FCSTD DOCUMENT  (FreeCAD 1.0R39109 (Git))
Label: 2020v
License: All rights reserved
LicenseURL: https://en.wikipedia.org/wiki/All_rights_reserved
objects: Sketcher::SketchObject×1
note: 2 computed .brp shape members not serialized (recipe doc carries the construction recipe); baked Part::Feature solids carry a one-line shape summary decoded from their .brp

FEATURE [Sketcher::SketchObject] Sketch
  ArcFitTolerance = 1e-06
  FullyConstrained = false
  MakeInternals = false
  sketch-geometry (57):
    g0: ArcOfCircle CenterX=-9.49927 CenterY=-9.49965 CenterZ=0 NormalX=0 NormalY=0 NormalZ=1 AngleXU=0 Radius=0.5 StartAngle=3.14159 EndAngle=4.71239
    g1: LineSegment StartX=-9.49927 StartY=-9.99965 StartZ=0 EndX=-4.57927 EndY=-9.99965 EndZ=0
    g2: LineSegment StartX=-4.57927 StartY=-9.99965 StartZ=0 EndX=-3.12427 EndY=-8.54465 EndZ=0
    g3: LineSegment StartX=-3.12427 StartY=-8.54465 StartZ=0 EndX=-3.12427 EndY=-8.19465 EndZ=0
    g4: LineSegment StartX=-3.12427 StartY=-8.19465 StartZ=0 EndX=-5.49927 EndY=-8.19465 EndZ=0
    g5: LineSegment StartX=-5.49927 StartY=-8.19465 StartZ=0 EndX=-5.49927 EndY=-6.55465 EndZ=0
    g6: LineSegment StartX=-5.49927 StartY=-6.55465 StartZ=0 EndX=-2.84427 EndY=-3.89965 EndZ=0
    g7: LineSegment StartX=-2.84427 StartY=-3.89965 StartZ=0 EndX=2.84573 EndY=-3.89965 EndZ=0
    g8: LineSegment StartX=2.84573 StartY=-3.89965 StartZ=0 EndX=5.50073 EndY=-6.55465 EndZ=0
    g9: LineSegment StartX=5.50073 StartY=-6.55465 StartZ=0 EndX=5.50073 EndY=-8.19465 EndZ=0
    g10: LineSegment StartX=5.50073 StartY=-8.19465 StartZ=0 EndX=3.12573 EndY=-8.19465 EndZ=0
    g11: LineSegment StartX=3.12573 StartY=-8.19465 StartZ=0 EndX=3.12573 EndY=-8.54465 EndZ=0
    g12: LineSegment StartX=3.12573 StartY=-8.54465 StartZ=0 EndX=4.58073 EndY=-9.99965 EndZ=0
    g13: LineSegment StartX=4.58073 StartY=-9.99965 StartZ=0 EndX=9.50073 EndY=-9.99965 EndZ=0
    g14: ArcOfCircle CenterX=9.50073 CenterY=-9.49965 CenterZ=0 NormalX=0 NormalY=0 NormalZ=1 AngleXU=0 Radius=0.5 StartAngle=4.71239 EndAngle=6.28319
    g15: LineSegment StartX=10.0007 StartY=-9.49965 StartZ=0 EndX=10.0007 EndY=-4.57965 EndZ=0
    g16: LineSegment StartX=10.0007 StartY=-4.57965 StartZ=0 EndX=8.54573 EndY=-3.12465 EndZ=0
    g17: LineSegment StartX=8.54573 StartY=-3.12465 StartZ=0 EndX=8.19573 EndY=-3.12465 EndZ=0
    g18: LineSegment StartX=8.19573 StartY=-3.12465 StartZ=0 EndX=8.19573 EndY=-5.48833 EndZ=0
    g19: LineSegment StartX=8.19573 StartY=-5.48833 StartZ=0 EndX=6.55573 EndY=-5.48833 EndZ=0
    g20: LineSegment StartX=6.55573 StartY=-5.48833 StartZ=0 EndX=3.90073 EndY=-2.83333 EndZ=0
    g21: LineSegment StartX=3.90073 StartY=-2.83333 StartZ=0 EndX=3.90073 EndY=2.83403 EndZ=0
    g22: LineSegment StartX=3.90073 StartY=2.83403 StartZ=0 EndX=6.55573 EndY=5.48903 EndZ=0
    g23: LineSegment StartX=6.55573 StartY=5.48903 StartZ=0 EndX=8.19573 EndY=5.48903 EndZ=0
    g24: LineSegment StartX=8.19573 StartY=5.48903 StartZ=0 EndX=8.20867 EndY=3.12535 EndZ=0
    g25: LineSegment StartX=8.20867 StartY=3.12535 StartZ=0 EndX=8.54573 EndY=3.12535 EndZ=0
    g26: LineSegment StartX=8.54573 StartY=3.12535 StartZ=0 EndX=10.0007 EndY=4.58035 EndZ=0
    g27: LineSegment StartX=10.0007 StartY=4.58035 StartZ=0 EndX=10.0007 EndY=9.50035 EndZ=0
    g28: ArcOfCircle CenterX=9.50073 CenterY=9.50035 CenterZ=0 NormalX=0 NormalY=0 NormalZ=1 AngleXU=0 Radius=0.5 StartAngle=0 EndAngle=1.5708
    g29: LineSegment StartX=9.50073 StartY=10.0003 StartZ=0 EndX=4.58073 EndY=10.0003 EndZ=0
    g30: LineSegment StartX=4.58073 StartY=10.0003 StartZ=0 EndX=3.12573 EndY=8.54535 EndZ=0
    g31: LineSegment StartX=3.12573 StartY=8.54535 StartZ=0 EndX=3.12573 EndY=8.19535 EndZ=0
    g32: LineSegment StartX=3.12573 StartY=8.19535 StartZ=0 EndX=5.50073 EndY=8.19535 EndZ=0
    g33: LineSegment StartX=5.50073 StartY=8.19535 StartZ=0 EndX=5.50073 EndY=6.55535 EndZ=0
    g34: LineSegment StartX=5.50073 StartY=6.55535 StartZ=0 EndX=2.84573 EndY=3.90035 EndZ=0
    g35: LineSegment StartX=2.84573 StartY=3.90035 StartZ=0 EndX=-2.84427 EndY=3.90035 EndZ=0
    g36: LineSegment StartX=-2.84427 StartY=3.90035 StartZ=0 EndX=-5.49927 EndY=6.55535 EndZ=0
    g37: LineSegment StartX=-5.49927 StartY=6.55535 StartZ=0 EndX=-5.49927 EndY=8.19535 EndZ=0
    g38: LineSegment StartX=-5.49927 StartY=8.19535 StartZ=0 EndX=-3.12427 EndY=8.19535 EndZ=0
    g39: LineSegment StartX=-3.12427 StartY=8.19535 StartZ=0 EndX=-3.12427 EndY=8.54535 EndZ=0
    g40: LineSegment StartX=-3.12427 StartY=8.54535 StartZ=0 EndX=-4.57927 EndY=10.0003 EndZ=0
    g41: LineSegment StartX=-4.57927 StartY=10.0003 StartZ=0 EndX=-9.49927 EndY=10.0003 EndZ=0
    g42: ArcOfCircle CenterX=-9.49927 CenterY=9.50035 CenterZ=0 NormalX=0 NormalY=0 NormalZ=1 AngleXU=0 Radius=0.5 StartAngle=1.5708 EndAngle=3.14159
    g43: LineSegment StartX=-9.99927 StartY=9.50035 StartZ=0 EndX=-9.99927 EndY=4.58035 EndZ=0
    g44: LineSegment StartX=-9.99927 StartY=4.58035 StartZ=0 EndX=-8.54427 EndY=3.12535 EndZ=0
    g45: LineSegment StartX=-8.54427 StartY=3.12535 StartZ=0 EndX=-8.19427 EndY=3.12535 EndZ=0
    g46: LineSegment StartX=-8.19427 StartY=3.12535 StartZ=0 EndX=-8.19427 EndY=5.48903 EndZ=0
    g47: LineSegment StartX=-8.19427 StartY=5.48903 StartZ=0 EndX=-6.55427 EndY=5.48903 EndZ=0
    g48: LineSegment StartX=-6.55427 StartY=5.48903 StartZ=0 EndX=-3.89927 EndY=2.83403 EndZ=0
    g49: LineSegment StartX=-3.89927 StartY=2.83403 StartZ=0 EndX=-3.89927 EndY=-2.83333 EndZ=0
    g50: LineSegment StartX=-3.89927 StartY=-2.83333 StartZ=0 EndX=-6.55427 EndY=-5.48833 EndZ=0
    g51: LineSegment StartX=-6.55427 StartY=-5.48833 StartZ=0 EndX=-8.19427 EndY=-5.48833 EndZ=0
    g52: LineSegment StartX=-8.19427 StartY=-5.48833 StartZ=0 EndX=-8.19427 EndY=-3.12465 EndZ=0
    g53: LineSegment StartX=-8.19427 StartY=-3.12465 StartZ=0 EndX=-8.54427 EndY=-3.12465 EndZ=0
    g54: LineSegment StartX=-8.54427 StartY=-3.12465 StartZ=0 EndX=-9.99927 EndY=-4.57965 EndZ=0
    g55: LineSegment StartX=-9.99927 StartY=-4.57965 StartZ=0 EndX=-9.99927 EndY=-9.49965 EndZ=0
    g56: Circle CenterX=0.000729931 CenterY=0.000348339 CenterZ=0 NormalX=0 NormalY=0 NormalZ=-1 AngleXU=0 Radius=2.1
